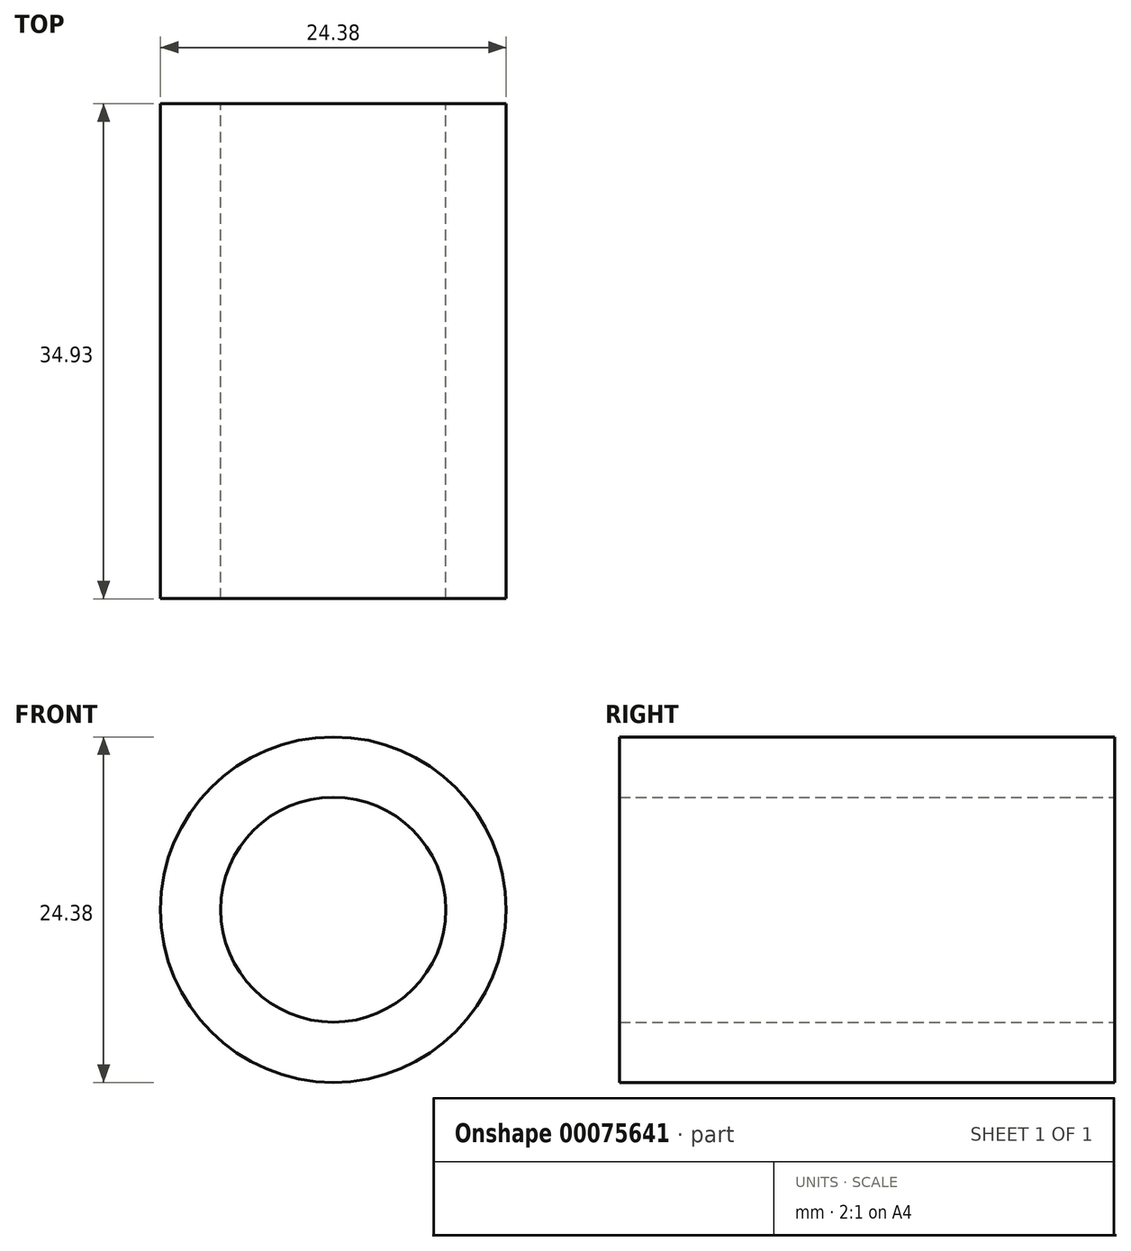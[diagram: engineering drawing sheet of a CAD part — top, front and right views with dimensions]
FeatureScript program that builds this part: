
annotation { "Feature Type Name" : "Feature", "Feature Type Description" : "" }
export const myFeature = defineFeature(function(context is Context, id is Id, definition is map)
    precondition{}
    {
        {
            var Q0;
            Q0=qCreatedBy(makeId("Front.planeOp"),FACE);
            var sketch = newSketch(context, id + "F0", { "sketchPlane" : qUnion([Q0])});
            skCircle(sketch, "E0", {"center": v(0, 0) * mm, "radius": 12.2 * mm});
            skCircle(sketch, "E1", {"center": v(0, 0) * mm, "radius": 7.94 * mm});
            skSolve(sketch);
        }
        {
            var Q0;
            Q0=makeQuery(id+"F0.imprint","IMPRINT",FACE,{"disambiguationData":[TD([[makeQuery(id+"F0.imprint","IMPRINT",EDGE,{"derivedFrom":sQuery(id+"F0.wireOp",EDGE,"E0")}),1.0]])]});
            extrude(context, id + "F1", {"entities" : qUnion([Q0]), "depth" : 34.92 * mm});
        }
    });
